# Revit family: FS_Цветочница_Гран-При_R16
name_source: partatom
category: Антураж
revit_build: Autodesk Revit 2016 (Build: 20160314_0715(x64)
units: mm (PartAtom-declared; Revit-internal decimal feet)

## family parameters
Всегда вертикально = Да
Источник визуального образа = Геометрия семейства
На основе рабочей плоскости = Нет
Общий = Нет
При загрузке вырезать с полостями = Нет
Точка расчета площади = Нет

## types (4) — shared parameters
ADSK_Код изделия = 8445
ADSK_Наименование = Цветочница «Гран-При» 11 горшков
URL = https://hobbyka.ru
Высота = 800 мм
Изготовитель = ООО 'Хоббика'
Комментарии к типоразмеру = Материал: стеклопластиковый композит с гранитной крошкой

## per-type parameters (varying)
| type | 1 | 2 | 3 | 4 | ADSK_Материал опоры | Положение | Стоимость | Центр_2 | Центр_3 | Центр_4 | Центр_6 |
| Цветочница «Гран-При» 11 горшков | Да | Нет | Нет | Нет | <По категории> | 225 мм | 65780 $ | Да | Нет | Нет | Нет |
| Цветочница «Гран-При» 16 горшков | Нет | Да | Нет | Нет | <По категории> | 225 мм | 97290 $ | Нет | Да | Нет | Нет |
| Цветочница «Гран-При» 21 горшков | Да | Нет | Да | Нет | <По категории> | 245 мм | 121440 $ | Нет | Нет | Да | Нет |
| Цветочница «Гран-При» 31 горшков | Да | Да | Нет | Да | Камень | 400 мм | 182045 $ | Нет | Нет | Нет | Да |
